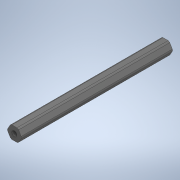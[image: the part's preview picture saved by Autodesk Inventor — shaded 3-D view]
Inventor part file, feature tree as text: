
AUTODESK INVENTOR PART (.ipt)
format: ipt  version: 2020 (Build 240168000, 168)  size: 137,728 bytes
history: native  units: in
note: dims shown in document units (in); Inventor stores cm internally (conversion verified against a paired STEP export)
features: plane x1, extrude x1, sketch x1, other x1
ambient origin geometry x8: Origin, YZ Plane, XZ Plane, XY Plane, X Axis, Y Axis, Z Axis, Center Point
bodies: Solid1 (feature_tree)
feature tree (4):
  plane  "Work Plane1"
  extrude  "Extrusion1"  Depth=1.0in
  sketch  "Sketch1"  dims[d0=-6.0in d1=1.0in d2=1.0in d3=2.0in d4=2.0in d5=27.0in d6=0.0in]
  other  "Cut-Extrude2"
